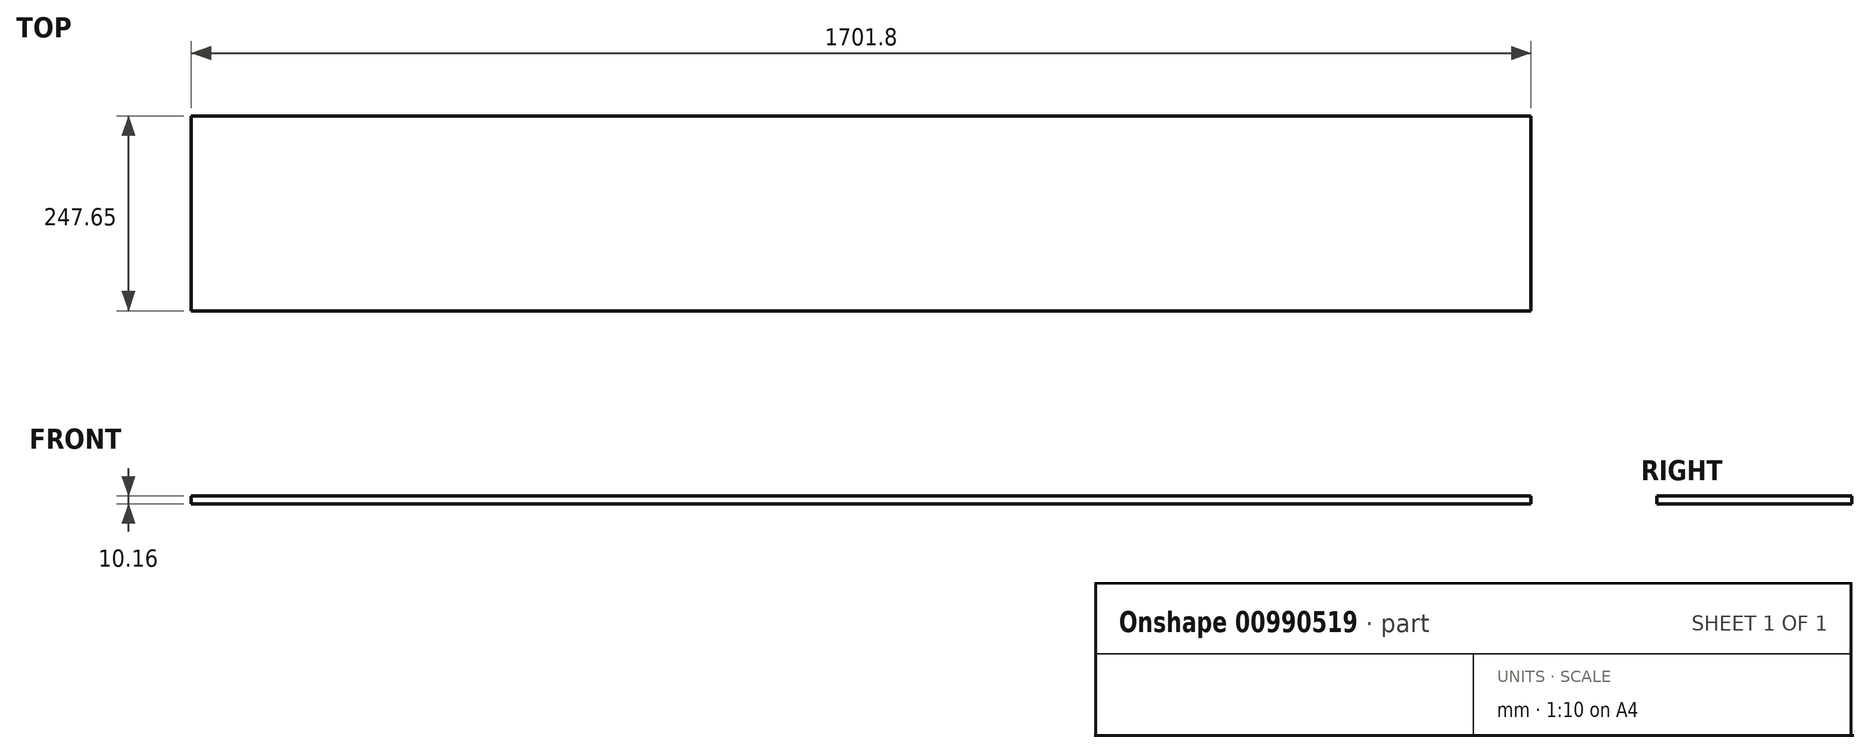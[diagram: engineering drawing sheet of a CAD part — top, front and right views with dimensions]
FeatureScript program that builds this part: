
annotation { "Feature Type Name" : "Feature", "Feature Type Description" : "" }
export const myFeature = defineFeature(function(context is Context, id is Id, definition is map)
    precondition{}
    {
        {
            var Q0;
            Q0=qCreatedBy(makeId("Top.planeOp"),FACE);
            var sketch = newSketch(context, id + "F0", { "sketchPlane" : qUnion([Q0])});
            skLineSegment(sketch, "E0.bottom", {"start": v(-742.4, 87.95) * mm, "end": v(959.4, 87.95) * mm});
            skLineSegment(sketch, "E0.top", {"start": v(-742.4, -159.7) * mm, "end": v(959.4, -159.7) * mm});
            skLineSegment(sketch, "E0.left", {"start": v(-742.4, 87.95) * mm, "end": v(-742.4, -159.7) * mm});
            skLineSegment(sketch, "E0.right", {"start": v(959.4, 87.95) * mm, "end": v(959.4, -159.7) * mm});
            skSolve(sketch);
        }
        {
            var Q0;
            Q0 = qSketchRegion(id + "F0", true);
            extrude(context, id + "F1", {"entities" : qUnion([Q0]), "depth" : 10.16 * mm, "offsetDistance" : 25.4 * mm});
        }
    });
